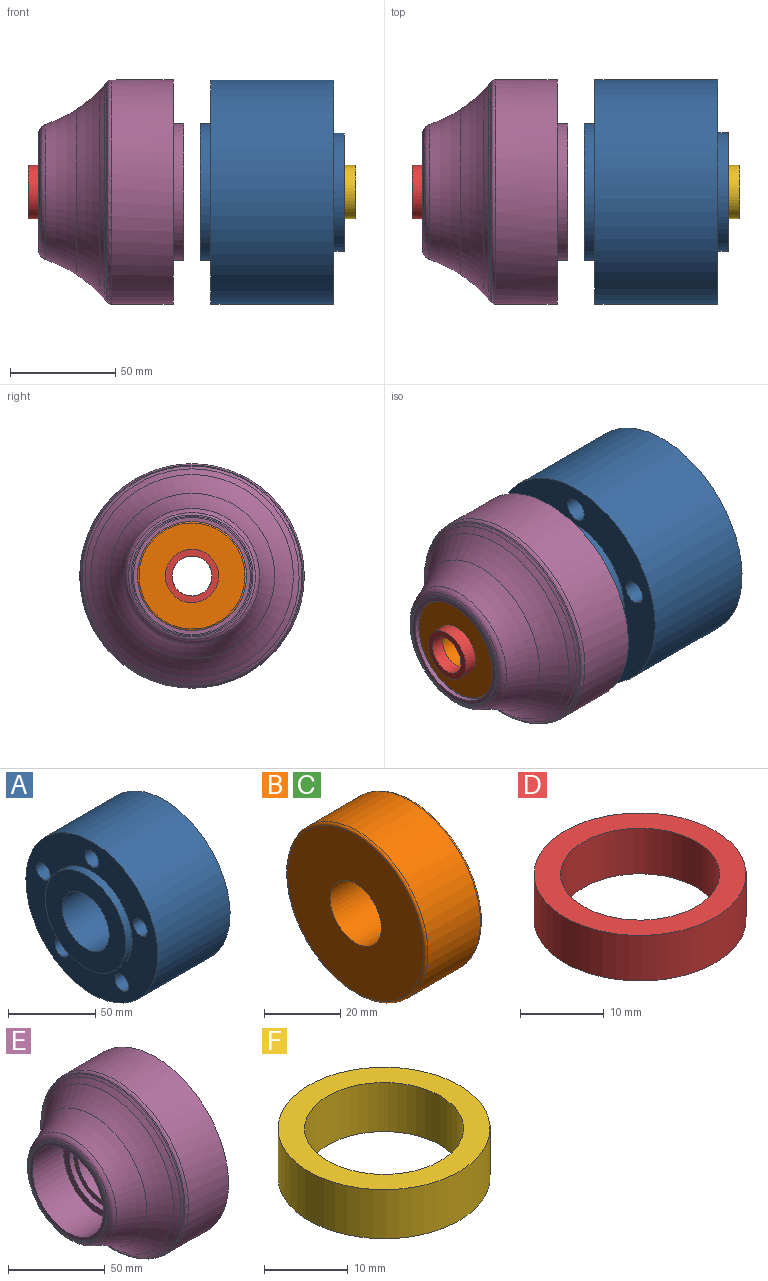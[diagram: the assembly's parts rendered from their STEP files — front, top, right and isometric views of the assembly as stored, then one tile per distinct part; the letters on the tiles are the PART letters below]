
ASSEMBLY  parts=6 mates=10
PART A: 37 faces, bbox 68.6x106.8x106.8 mm
  f0: cone r=0mm half-angle=59deg, axis (1,0,0), area 39mm2, adj f1
  f1: cylinder r=3.26mm len=44.18mm, axis (1,0,0), area 906.1mm2, adj f0,f23
  f2: cylinder r=5.56mm len=16.15mm, axis (1,0,0), area 564mm2, adj f3,f25
  f3: plane 17.46x17.46mm, normal (1,0,0), area 142.5mm2, adj f2,f4
  f4: cylinder r=8.73mm len=42.29mm, axis (1,0,0), area 2320.1mm2, adj f3,f23
  f5: cone r=0mm half-angle=59deg, axis (1,0,0), area 39mm2, adj f6
  f6: cylinder r=3.26mm len=44.18mm, axis (1,0,0), area 906.1mm2, adj f5,f23
  f7: cylinder r=5.56mm len=16.15mm, axis (1,0,0), area 564mm2, adj f8,f25
  f8: plane 17.46x17.46mm, normal (1,0,0), area 142.5mm2, adj f7,f9
  f9: cylinder r=8.73mm len=42.29mm, axis (1,0,0), area 2320.1mm2, adj f8,f23
  f10: cone r=0mm half-angle=59deg, axis (1,0,0), area 39mm2, adj f11
  f11: cylinder r=3.26mm len=44.18mm, axis (1,0,0), area 906.1mm2, adj f10,f23
  f12: cylinder r=5.56mm len=16.15mm, axis (1,0,0), area 564mm2, adj f13,f25
  f13: plane 17.46x17.46mm, normal (1,0,0), area 142.5mm2, adj f12,f14
  f14: cylinder r=8.73mm len=42.29mm, axis (1,0,0), area 2320.1mm2, adj f13,f23
  f15: cone r=0mm half-angle=59deg, axis (1,0,0), area 39mm2, adj f16
  f16: cylinder r=3.26mm len=44.18mm, axis (1,0,0), area 906.1mm2, adj f15,f23
  f17: cylinder r=5.56mm len=16.15mm, axis (1,0,0), area 564mm2, adj f18,f25
  f18: plane 17.46x17.46mm, normal (1,0,0), area 142.5mm2, adj f17,f19
  f19: cylinder r=8.73mm len=42.29mm, axis (1,0,0), area 2320.1mm2, adj f18,f23
  f20: cylinder r=25.97mm len=51.94mm, axis (1,0,0), area 3730.4mm2, adj f21,f31
  f21: plane 56.26x56.26mm, normal (1,0,0), area 367mm2, adj f20,f22
  f22: cylinder r=28.13mm len=56.26mm, axis (1,0,0), area 897.9mm2, adj f21,f23
  f23: plane 106.81x106.81mm, normal (1,0,0), area 5108.8mm2, adj f1,f4,f6,f9,f11,f14,f16,f19
  f24: cylinder r=53.4mm len=106.81mm, axis (1,0,0), area 19611mm2, adj f23,f25
  f25: plane 106.81x106.81mm, normal (-1,0,0), area 5133.1mm2, adj f2,f7,f12,f17,f24,f26,f32
  f26: cylinder r=32.61mm len=65.23mm, axis (1,0,0), area 1041mm2, adj f25,f27
  f27: plane 65.23x65.23mm, normal (-1,0,0), area 2201.5mm2, adj f26,f28
  f28: cylinder r=19.05mm len=42.56mm, axis (1,0,0), area 5094.7mm2, adj f27,f29
  f29: plane 43.94x43.94mm, normal (1,0,0), area 376.5mm2, adj f28,f30
  f30: cylinder r=21.97mm len=43.94mm, axis (1,0,0), area 439.2mm2, adj f29,f31
  f31: plane 51.94x51.94mm, normal (1,0,0), area 602.5mm2, adj f20,f30
  f32: cylinder r=5.56mm len=16.15mm, axis (1,0,0), area 564mm2, adj f25,f33
  f33: plane 17.46x17.46mm, normal (1,0,0), area 142.5mm2, adj f32,f34
  f34: cylinder r=8.73mm len=42.29mm, axis (1,0,0), area 2320.1mm2, adj f23,f33
  f35: cone r=0mm half-angle=59deg, axis (1,0,0), area 39mm2, adj f36
  f36: cylinder r=3.26mm len=44.18mm, axis (1,0,0), area 906.1mm2, adj f23,f35
PART B: 6 faces, bbox 21x56.3x56.3 mm
  f0: plane 50.48x50.48mm, normal (1,0,0), area 1716mm2, adj f3,f4
  f1: cylinder r=26mm len=52mm, axis (1,0,0), area 3174.3mm2, adj f4,f5
  f2: plane 50.48x50.48mm, normal (-1,0,0), area 1716mm2, adj f3,f5
  f3: cylinder r=9.53mm len=20.96mm, axis (1,0,0), area 1254.1mm2, adj f0,f2
  f4: torus R=25.24mm, axis (-1,0,0), area 193.5mm2, adj f0,f1
  f5: torus R=25.24mm, axis (-1,0,0), area 193.5mm2, adj f1,f2
PART C: same geometry as B
PART D: 4 faces, bbox 25.4x25.4x6.7 mm
  f0: cylinder r=9.53mm len=19.05mm, axis (0,0,1), area 399.8mm2, adj f2,f3
  f1: cylinder r=12.7mm len=25.4mm, axis (0,0,1), area 533.1mm2, adj f2,f3
  f2: plane 25.4x25.4mm, normal (0,0,-1), area 221.7mm2, adj f0,f1
  f3: plane 25.4x25.4mm, normal (0,0,1), area 221.7mm2, adj f0,f1
PART E: 30 faces, bbox 85x197.1x197.1 mm
  f0: cylinder r=53.4mm len=106.8mm, axis (1,0,0), area 9801.5mm2, adj f3,f17
  f1: cylinder r=19.04mm len=43.07mm, axis (1,0,0), area 5153.4mm2, adj f15,f19
  f2: cylinder r=21.96mm len=43.93mm, axis (1,0,0), area 439mm2, adj f15,f16
  f3: torus R=50.18mm, axis (1,0,0), area 711.9mm2, adj f0,f4
  f4: torus R=50.1mm, axis (1,0,0), area 198.3mm2, adj f3,f5
  f5: cone r=52.29mm half-angle=50.2deg, axis (1,0,0), area 547.7mm2, adj f4,f6
  f6: torus R=90.33mm, axis (1,0,0), area 1153.1mm2, adj f5,f7
  f7: torus R=91.07mm, axis (1,0,0), area 3826.9mm2, adj f6,f8
  f8: torus R=91.03mm, axis (1,0,0), area 3680.4mm2, adj f7,f9
  f9: torus R=27.61mm, axis (1,0,0), area 647.7mm2, adj f8,f10
  f10: torus R=27.59mm, axis (1,0,0), area 237.1mm2, adj f9,f11
  f11: torus R=27.74mm, axis (1,0,0), area 117.3mm2, adj f10,f12
  f12: cone r=28.4mm half-angle=83.9deg, axis (1,0,0), area 99.1mm2, adj f11,f13
  f13: cone r=27.84mm half-angle=89.9deg, axis (1,0,0), area 317.8mm2, adj f12,f14
  f14: cylinder r=25.96mm len=51.92mm, axis (1,0,0), area 3729mm2, adj f13,f16
  f15: plane 43.93x43.93mm, normal (-1,0,0), area 376.2mm2, adj f1,f2
  f16: plane 51.92x51.92mm, normal (-1,0,0), area 602mm2, adj f2,f14
  f17: plane 106.8x106.8mm, normal (1,0,0), area 5234mm2, adj f0,f18,f21,f23,f25,f27,f29
  f18: cylinder r=32.6mm len=65.2mm, axis (-1,0,0), area 1040.5mm2, adj f17,f19
  f19: plane 65.2x65.2mm, normal (1,0,0), area 2199.5mm2, adj f1,f18
  f20: cone r=0mm half-angle=59deg, axis (1,0,0), area 90.2mm2, adj f21
  f21: cylinder r=4.96mm len=26.79mm, axis (1,0,0), area 835.1mm2, adj f17,f20
  f22: cone r=0mm half-angle=59deg, axis (1,0,0), area 90.2mm2, adj f23
  f23: cylinder r=4.96mm len=26.79mm, axis (1,0,0), area 835.1mm2, adj f17,f22
  f24: cone r=0mm half-angle=59deg, axis (1,0,0), area 90.2mm2, adj f25
  f25: cylinder r=4.96mm len=26.79mm, axis (1,0,0), area 835.1mm2, adj f17,f24
  f26: cone r=0mm half-angle=59deg, axis (1,0,0), area 90.2mm2, adj f27
  f27: cylinder r=4.96mm len=26.79mm, axis (1,0,0), area 835.1mm2, adj f17,f26
  f28: cone r=0mm half-angle=59deg, axis (1,0,0), area 90.2mm2, adj f29
  f29: cylinder r=4.96mm len=26.79mm, axis (1,0,0), area 835.1mm2, adj f17,f28
PART F: 4 faces, bbox 25.4x25.4x7.2 mm
  f0: cylinder r=9.53mm len=19.05mm, axis (0,0,1), area 430.2mm2, adj f2,f3
  f1: cylinder r=12.7mm len=25.4mm, axis (0,0,1), area 573.6mm2, adj f2,f3
  f2: plane 25.4x25.4mm, normal (0,0,-1), area 221.7mm2, adj f0,f1
  f3: plane 25.4x25.4mm, normal (0,0,1), area 221.7mm2, adj f0,f1
PLACE A rot(axis=(1,0,0),0deg) t=(65.18,0,0)mm
PLACE B rot(axis=(-1,0,0),22.5deg) t=(-57.56,0,0)mm
PLACE C t=(63.27,0,0)mm
PLACE D rot(axis=(-0.19,0.96,-0.19),92.2deg) t=(-78.51,0,0)mm
PLACE E at identity fixed
PLACE F rot(axis=(0.71,0,-0.71),180deg) t=(63.27,0,0)mm
MATE fastened E.f0 <-> A.f20  axis (1,0,0) through (-16.38,0,0)mm
MATE cylindrical B.f1 <-> E.f0  axis (1,0,0) through (-68.03,0,0)mm
MATE cylindrical D.f0 <-> B.f1  axis (1,0,0) through (-78.51,0,0)mm
MATE cylindrical A.f20 <-> C.f1  axis (1,0,0) through (65.18,0,0)mm
MATE cylindrical F.f1 <-> A.f20  axis (-1,0,0) through (63.27,0,0)mm
MATE planar B.f1 <-> D.f1  axis (-1,0,0) through (-78.51,0,0)mm
MATE cylindrical A.f20 <-> E.f0  axis (-1,0,0) through (-3.43,0,0)mm
MATE planar E.f0 <-> B.f1  axis (-1,0,0) through (-57.56,0,0)mm
MATE planar F.f1 <-> C.f1  axis (-1,0,0) through (63.27,0,0)mm
MATE planar A.f20 <-> C.f1  axis (1,0,0) through (42.32,0,0)mm
